# Revit family: BC_Hitachi_RAS3-HVNP1E_LOD200
name_source: partatom
category: Equipement de génie climatique
revit_build: Autodesk Revit 2016 (Build: 20150220_1215(x64)
units: mm (PartAtom-declared; Revit-internal decimal feet)

## family parameters
Basée sur le plan de construction = Non
Cote de connecteur circulaire = Utiliser le diamètre
Couper avec des vides une fois chargée = Non
Numéro OmniClass = 23.75.00.00
Partagée = Non
Point de calcul de pièce = Non
Titre OmniClass = Climate Control (HVAC)
Toujours verticalement = Oui
Type d'élément = Normal

## types (1)
- RAS-3HVNP1E
    Coefficient Of Performance (COP) = 4.88
    Commentaires du type = RAS-3HVNP1E
    Cooling Capacity = 7 kW
    Description = The CENTRIFUGE IVX solution has been created for integrate this outdoor group inside the building
    Energy Efficiency Ratio (EER) = 4.49
    Fabricant = HITACHI
    Fan diameter = 600.00 mm
    Frequency = 50 Hz
    Gas Diameter = 15.88 mm
    Heating Capacity = 8 kW
    Height Gas pipe = 232.09 mm
    Height liquid pipe = 315.09 mm
    Liquid Diameter = 9.52 mm
    Mass = 103.00 kg
    Maximum AC Voltage = 253 V
    Maximum Air Flow = 45000.0 L/min
    Maximum Connected Capacity (%) = 120
    Maximum Input Power = 5 kW
    Minimum AC Voltage = 207 V
    Minimum Connected Capacity (%) = 50
    Modèle = Outdoor Unit - IVX Premium
    Nominal Current = 22 A
    Nominal Voltage = 230 V
    Nominal cooling capacity (max) = 8 kW
    Nominal cooling capacity (min) = 3 kW
    Nominal cooling power input = 1 kW
    Nominal heating capacity (max) = 11 kW
    Nominal heating capacity (min) = 4 kW
    Nominal heating power input = 2 kW
    Number of Poles = 1
    Overall Depth = 370.00 mm
    Overall Height = 800.00 mm
    Overall Width = 950.00 mm
    Product Code = 7E304018
    Recommended circuit breaker = 20 A
    Refrigerant = R410A
    Refrigerant charge = 2.30 kg
    Running current cooling = 6 A
    Running current heating = 7 A
    Sound power at rated load (dB(A)) = 63
    Sound pressure level Night mode cooling (dB(A)) = 42
    Sound pressure level cooling (dB(A)) = 46
    Sound pressure level heating (dB(A)) = 48

## geometry (parser evidence)
native form markers: Blend x2
no freeform markers — native parametric forms only
